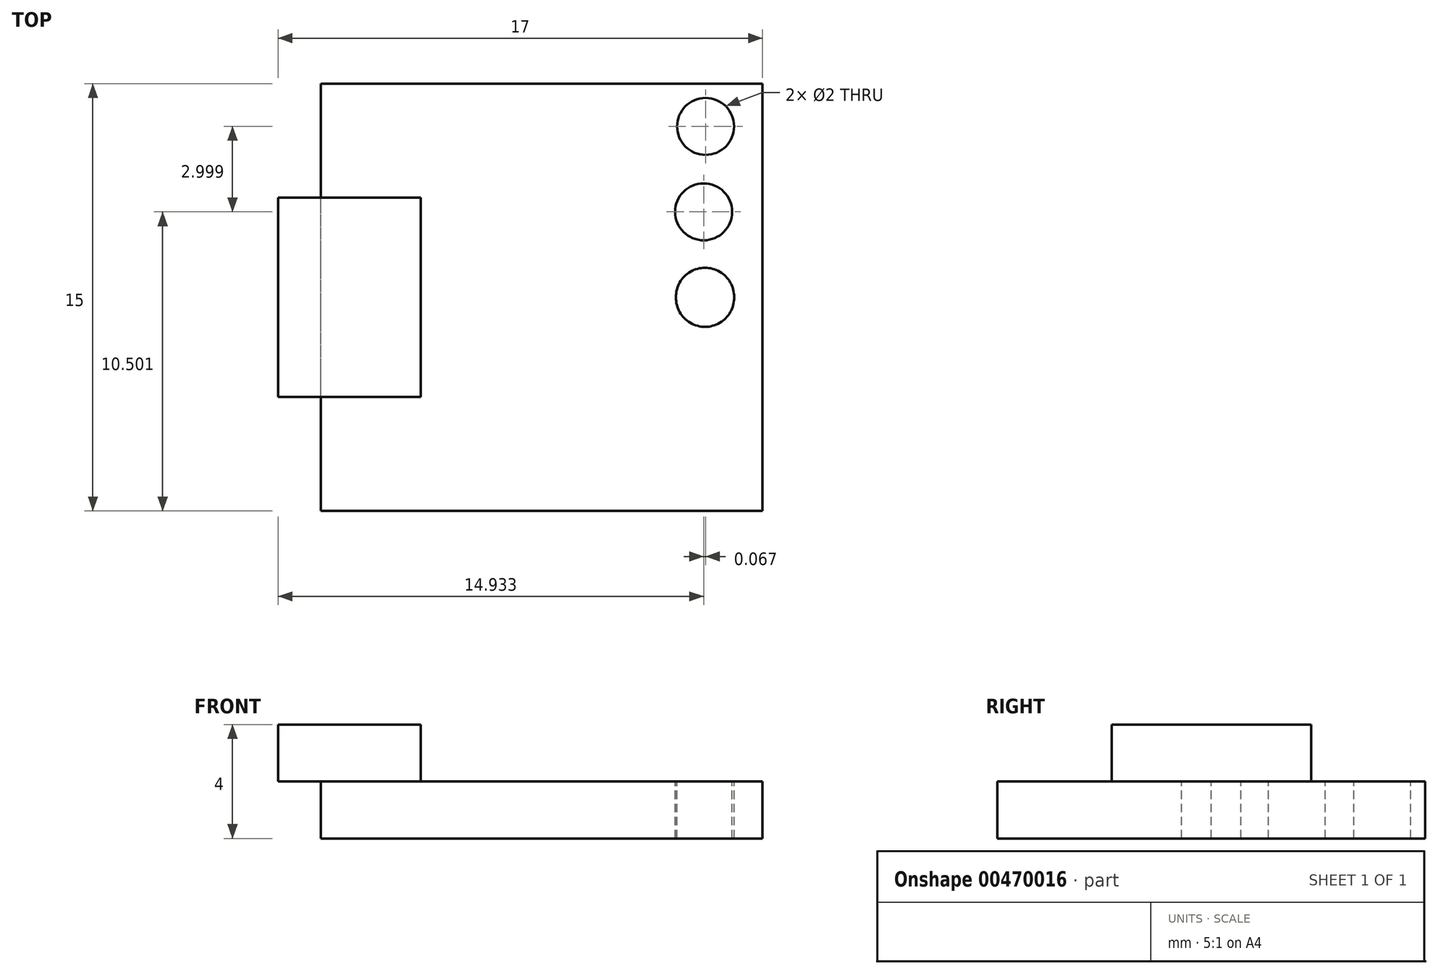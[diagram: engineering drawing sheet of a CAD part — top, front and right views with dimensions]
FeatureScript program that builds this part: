
annotation { "Feature Type Name" : "Feature", "Feature Type Description" : "" }
export const myFeature = defineFeature(function(context is Context, id is Id, definition is map)
    precondition{}
    {
        {
            var Q0;
            Q0=qCreatedBy(makeId("Top.planeOp"),FACE);
            var sketch = newSketch(context, id + "F0", { "sketchPlane" : qUnion([Q0])});
            skLineSegment(sketch, "E0.bottom", {"start": v(7.75, -7.5) * mm, "end": v(-7.75, -7.5) * mm});
            skLineSegment(sketch, "E0.top", {"start": v(7.75, 7.5) * mm, "end": v(-7.75, 7.5) * mm});
            skLineSegment(sketch, "E0.left", {"start": v(7.75, -7.5) * mm, "end": v(7.75, 7.5) * mm});
            skLineSegment(sketch, "E0.right", {"start": v(-7.75, -7.5) * mm, "end": v(-7.75, 7.5) * mm});
            skPoint(sketch, "E0.middle", {"position": v(0, 0) * mm});
            skSolve(sketch);
        }
        {
            var Q0;
            Q0 = qSketchRegion(id + "F0", true);
            extrude(context, id + "F1", {"entities" : qUnion([Q0]), "depth" : 2 * mm, "offsetDistance" : 25 * mm});
        }
        {
            var Q0;
            Q0=qCreatedBy(makeId("Top.planeOp"),FACE);
            cPlane(context, id + "F2", {"entities" : qUnion([Q0]), "cplaneType" : CPlaneType.OFFSET, "offset" : 2 * mm, "width" : 150 * mm, "height" : 150 * mm});
        }
        {
            var Q0;
            Q0=qCreatedBy(id+"F2.planeOp",FACE);
            var sketch = newSketch(context, id + "F3", { "sketchPlane" : qUnion([Q0])});
            skCircle(sketch, "E1", {"center": v(5.75, 6) * mm, "radius": 1 * mm});
            skCircle(sketch, "E2", {"center": v(5.68, 3) * mm, "radius": 1 * mm});
            skCircle(sketch, "E3", {"center": v(5.73, -0.02) * mm, "radius": 1.02 * mm});
            skCircle(sketch, "E4.MirrorC", {"center": v(5.73, 0.02) * mm, "radius": 1.02 * mm});
            skCircle(sketch, "E5.MirrorC", {"center": v(5.68, -3) * mm, "radius": 1 * mm});
            skCircle(sketch, "E6.MirrorC", {"center": v(5.75, -6) * mm, "radius": 1 * mm});
            skSolve(sketch);
        }
        {
            var Q0;
            Q0=makeQuery(id+"F3.imprint","IMPRINT",FACE,{"disambiguationData":[TD([[makeQuery(id+"F3.imprint","IMPRINT",EDGE,{"derivedFrom":sQuery(id+"F3.wireOp",EDGE,"E2")}),1.0]])]});
            var Q1;
            Q1=makeQuery(id+"F3.imprint","IMPRINT",FACE,{"disambiguationData":[TD([[makeQuery(id+"F3.imprint","IMPRINT",EDGE,{"derivedFrom":sQuery(id+"F3.wireOp",EDGE,"E5.MirrorC")}),-1.0]])]});
            var Q2;
            Q2=makeQuery(id+"F3.imprint","IMPRINT",FACE,{"disambiguationData":[TD([[makeQuery(id+"F3.imprint","IMPRINT",EDGE,{"derivedFrom":sQuery(id+"F3.wireOp",EDGE,"E6.MirrorC")}),-1.0]])]});
            var Q3;
            {var subQ0=sQuery(id+"F3.wireOp",EDGE,"E4.MirrorC");var subQ1=sQuery(id+"F3.wireOp",EDGE,"E3");var subQ2=makeQuery(id+"F3.imprint","INTERSECT",VERTEX,{"disambiguationData":[OD(0.0)],"derivedFrom":[subQ1,subQ0]});Q3=makeQuery(id+"F3.imprint","IMPRINT",FACE,{"disambiguationData":[TD([[makeQuery(id+"F3.imprint","IMPRINT",EDGE,{"disambiguationData":[TD([[subQ2,1.0]])],"derivedFrom":subQ1}),-1.0]])]});}
            var Q4;
            {var subQ0=sQuery(id+"F3.wireOp",EDGE,"E4.MirrorC");var subQ1=sQuery(id+"F3.wireOp",EDGE,"E3");var subQ2=makeQuery(id+"F3.imprint","INTERSECT",VERTEX,{"disambiguationData":[OD(0.0)],"derivedFrom":[subQ1,subQ0]});Q4=makeQuery(id+"F3.imprint","IMPRINT",FACE,{"disambiguationData":[TD([[makeQuery(id+"F3.imprint","IMPRINT",EDGE,{"disambiguationData":[TD([[subQ2,-1.0]])],"derivedFrom":subQ1}),1.0]])]});}
            var Q5;
            {var subQ0=sQuery(id+"F3.wireOp",EDGE,"E4.MirrorC");var subQ1=sQuery(id+"F3.wireOp",EDGE,"E3");var subQ2=makeQuery(id+"F3.imprint","INTERSECT",VERTEX,{"disambiguationData":[OD(0.0)],"derivedFrom":[subQ1,subQ0]});Q5=makeQuery(id+"F3.imprint","IMPRINT",FACE,{"disambiguationData":[TD([[makeQuery(id+"F3.imprint","IMPRINT",EDGE,{"disambiguationData":[TD([[subQ2,1.0]])],"derivedFrom":subQ1}),1.0]])]});}
            var Q6;
            Q6=makeQuery(id+"F3.imprint","IMPRINT",FACE,{"disambiguationData":[TD([[makeQuery(id+"F3.imprint","IMPRINT",EDGE,{"derivedFrom":sQuery(id+"F3.wireOp",EDGE,"E1")}),1.0]])]});
            extrude(context, id + "F4", {"entities" : qUnion([Q0, Q1, Q2, Q3, Q4, Q5, Q6]), "operationType" : NewBodyOperationType.REMOVE, "oppositeDirection" : true, "depth" : 2 * mm, "offsetDistance" : 25 * mm});
        }
        {
            var Q0;
            Q0=qCreatedBy(id+"F2.planeOp",FACE);
            var sketch = newSketch(context, id + "F5", { "sketchPlane" : qUnion([Q0])});
            skLineSegment(sketch, "E7.bottom", {"start": v(-4.25, -3.5) * mm, "end": v(-9.25, -3.5) * mm});
            skLineSegment(sketch, "E7.top", {"start": v(-4.25, 3.5) * mm, "end": v(-9.25, 3.5) * mm});
            skLineSegment(sketch, "E7.left", {"start": v(-4.25, -3.5) * mm, "end": v(-4.25, 3.5) * mm});
            skLineSegment(sketch, "E7.right", {"start": v(-9.25, -3.5) * mm, "end": v(-9.25, 3.5) * mm});
            skPoint(sketch, "E7.middle", {"position": v(-6.75, 0) * mm});
            skSolve(sketch);
        }
        {
            var Q0;
            Q0=makeQuery(id+"F5.imprint","IMPRINT",FACE,{"disambiguationData":[TD([[makeQuery(id+"F5.imprint","IMPRINT",EDGE,{"derivedFrom":sQuery(id+"F5.wireOp",EDGE,"E7.bottom")}),-1.0]])]});
            extrude(context, id + "F6", {"entities" : qUnion([Q0]), "operationType" : NewBodyOperationType.ADD, "depth" : 2 * mm, "offsetDistance" : 25 * mm});
        }
    });
